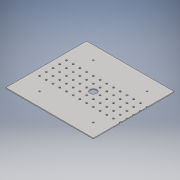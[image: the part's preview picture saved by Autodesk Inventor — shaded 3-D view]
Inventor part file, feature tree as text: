
AUTODESK INVENTOR PART (.ipt)
format: ipt  version: 2018 (Build 220112000, 112)  size: 243,200 bytes
history: native  units: in
note: dims shown in document units (in); Inventor stores cm internally (conversion verified against a paired STEP export)
features: extrude x5, sketch x5
ambient origin geometry x8: Origin, YZ Plane, XZ Plane, XY Plane, X Axis, Y Axis, Z Axis, Center Point
bodies: Solid1 (feature_tree)
feature tree (10):
  extrude  "Extrusion1"  Depth=0.125in
  extrude  "Extrusion2"  Depth=2.0in TaperAngle=0.0deg
  extrude  "Extrusion3"  Depth=0.25in
  extrude  "Extrusion4"  Depth=0.25in
  extrude  "Extrusion7"  Depth=12.0in TaperAngle=0.0deg
  sketch  "Sketch1"  dims[d2=0.125in d3=0.0in d4=6.0in]
  sketch  "Sketch2"  dims[d5=1.0in d6=2.0in d7=0.0in]
  sketch  "Sketch3"  dims[d9=0.25in d11=0.25in]
  sketch  "Sketch4"  dims[d12=0.25in d13=0.25in d14=0.25in d15=0.25in]
  sketch  "Sketch7"  dims[d18=0.25in d19=0.25in d20=0.25in d21=0.25in d22=0.25in d23=0.25in d24=0.25in d25=0.25in d26=0.25in d27=0.25in d28=0.25in d29=0.25in d33=0.25in d35=0.25in d36=0.25in d37=0.25in d38=0.25in d39=0.25in d41=0.25in d43=0.25in d44=0.25in d45=0.25in d46=0.25in d47=0.25in d48=2.0in d49=0.0in d54=1.0in d55=1.0in d56=0.25in d57=0.25in d59=2.0in d60=0.0in d73=13.0in d74=13.0in d75=12.0in d83=2.0in d84=3.0in d85=0.2031in d86=8.0in d87=8.0in d88=0.2031in d89=0.2031in d90=0.2031in d91=1.0in d92=0.0in]
